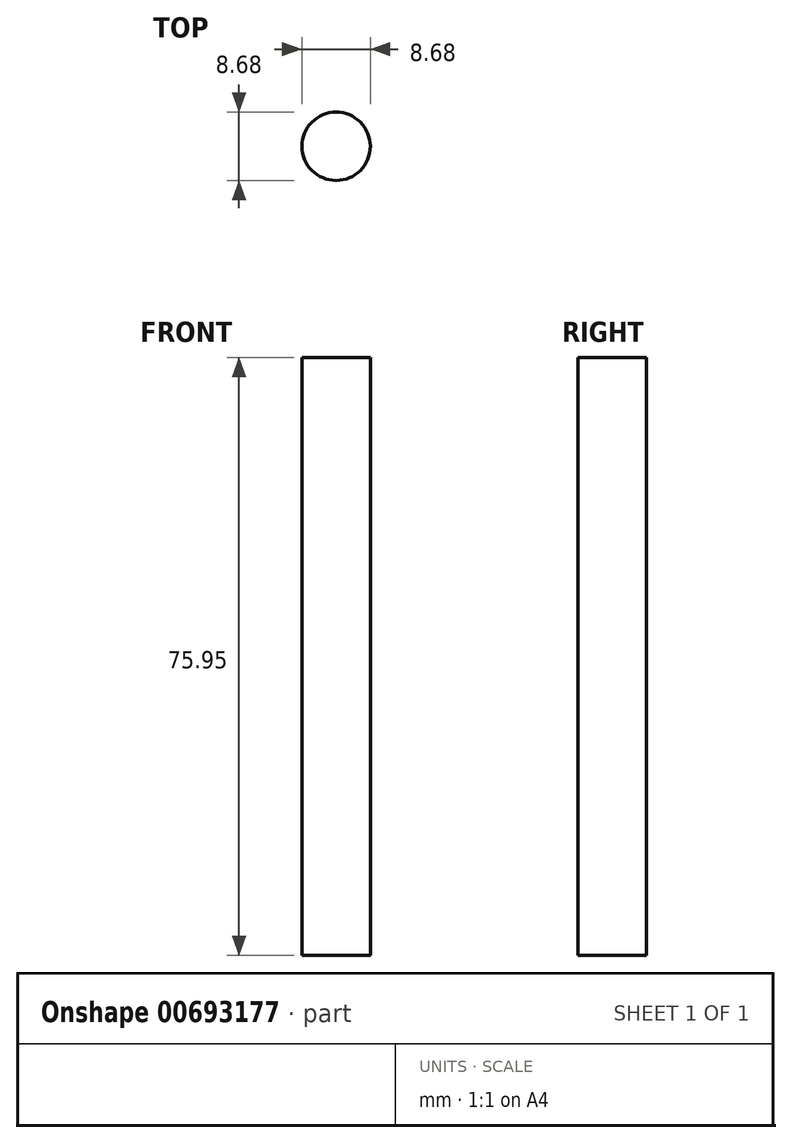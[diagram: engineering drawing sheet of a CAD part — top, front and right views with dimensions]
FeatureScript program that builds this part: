
annotation { "Feature Type Name" : "Feature", "Feature Type Description" : "" }
export const myFeature = defineFeature(function(context is Context, id is Id, definition is map)
    precondition{}
    {
        {
            var Q0;
            Q0=qCreatedBy(makeId("Top.planeOp"),FACE);
            var sketch = newSketch(context, id + "F0", { "sketchPlane" : qUnion([Q0])});
            skCircle(sketch, "E0", {"center": v(0, 0) * mm, "radius": 4.34 * mm});
            skSolve(sketch);
        }
        {
            var Q0;
            Q0 = qSketchRegion(id + "F0", true);
            extrude(context, id + "F1", {"entities" : qUnion([Q0]), "depth" : 75.95 * mm, "offsetDistance" : 25.4 * mm});
        }
    });
